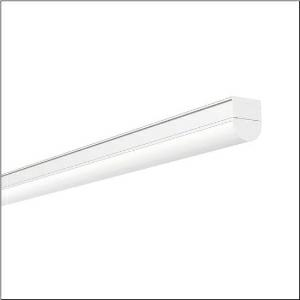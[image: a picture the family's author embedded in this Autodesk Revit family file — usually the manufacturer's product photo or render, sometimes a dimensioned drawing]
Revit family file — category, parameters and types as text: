
# Revit family: ecopack_r__31_51lj12mdm20a_29c1
name_source: partatom
category: Lighting Fixtures
units: mm (PartAtom-declared; Revit-internal decimal feet)

## family parameters
Cut with Voids When Loaded = No
Host = Face
Light Source = No
Part Type = Normal
Room Calculation Point = No
Round Connector Dimension = Use Diameter
Shared = No

## types (1)
- --- (1 x LED, 2510 lm, 20 W, 5000K)
    Apparent Load = 20 VA
    CIE Flux Codes = 41 71 90 93 100
    Color Rendering = 80
    Color Temperature = 5000K
    Default Elevation = 1800 mm
    Description = Ecopack® 31, diffuser luminaire, primary optical cover: cover, of PC, frosted, light emission: direct distribution, primary light characteristic: symmetric, installation type: surface-mounted, LED, rated luminous flux: 2.600lm, luminous efficacy: 130lm/W, light colour: 830/840/850, colour temperature: 3000/4000/5000K, control gear: ON/OFF Multilumen, with terminal, 3-pole, mains connection: 220..240V, AC, 50/60Hz, rated input power: 20W, housing, of aluminium, traffic white (RAL 9016), length: 600mm, width: 56mm, height: 68mm, end cap, of PC, white, protection rating (complete): IP20, insulation class (complete): insulation class I (protective earthing), certification: CE, impact resistance: IK06, permissible operating ambient temperature: -20..+40°C, packaging unit: 1 piece
    Height = 68 mm
    Lamp = 1 x LED
    Lamp Light Flux = 2510 lm
    Lamp Power = 20 W
    Lamp count = 1
    Length = 600 mm
    Luminous efficacy = 126 lm/W
    Manufacturer = Siteco
    ModVariant = No
    Model = 51LJ12MDM20A
    Mounting Place = Ceiling
    Mounting Type = Surface mounted
    Number of Poles = 1
    OnlyDefault = Yes
    Power Factor = 1
    Product Name = Ecopack® 31
    Product group = diffuser luminaire
    ProductGroupID = 306
    Protection Class = Protection class I
    Protection Degree = IP 20
    RLX_Detail_Level = 1
    RLX_Emergency_Light_Flux = 0 lm
    RLX_Emergency_Type = 0
    RLX_Emergency_Type_DB = No
    RlxData = <blob elided: 25661 chars, md5=4b189d8e>
    Socket = socket
    Standby Power = 0 W
    System Light Flux = 2510 lm
    System Power = 20 W
    Type Comments = individual setting: colour temperature 5000K, luminous flux: 100 % | (ON | ON)
    Type Image = l_1007030.jpg
    URL = http://relux.com
    VarID = @adj_174056
    Voltage = 0 V
    Weight = 0.00 kg
    Width = 56 mm

## geometry (parser evidence)
native form markers: Blend x4, Sweep x12
no freeform markers — native parametric forms only
